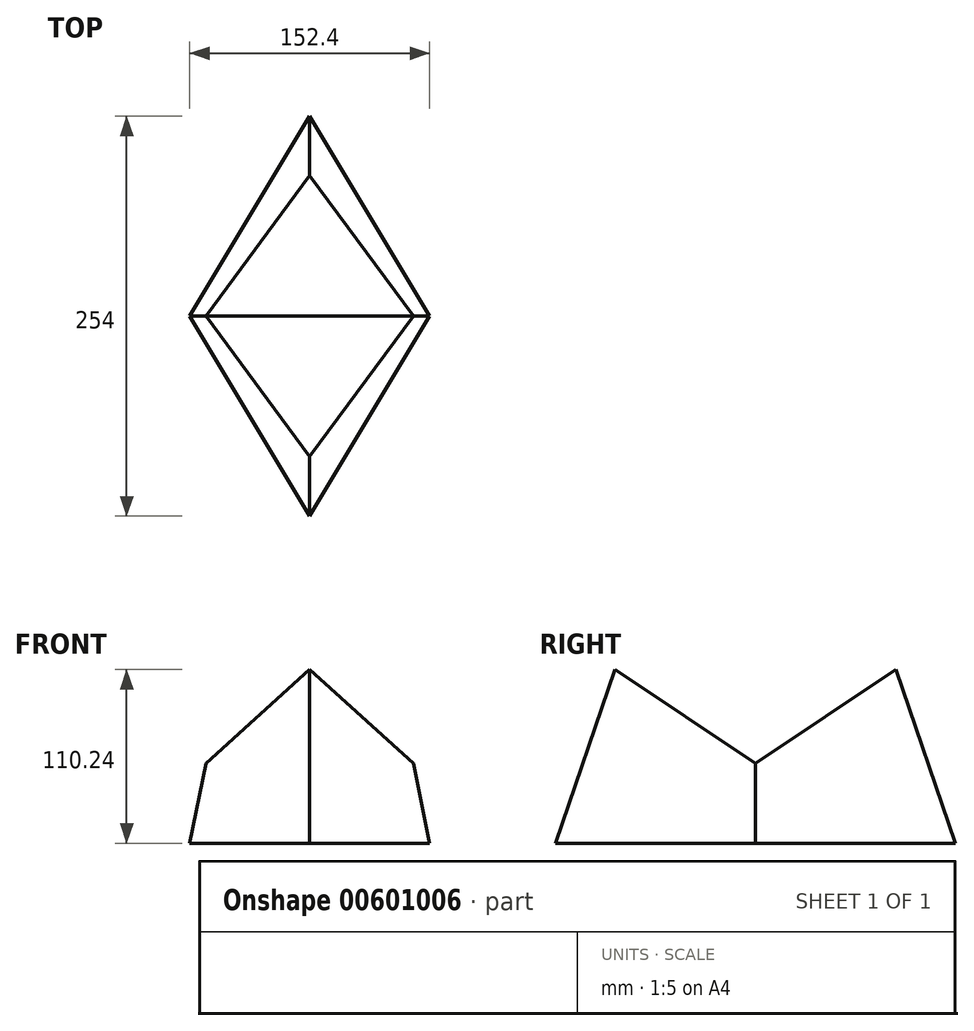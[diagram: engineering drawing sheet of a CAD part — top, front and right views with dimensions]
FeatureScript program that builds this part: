
annotation { "Feature Type Name" : "Feature", "Feature Type Description" : "" }
export const myFeature = defineFeature(function(context is Context, id is Id, definition is map)
    precondition{}
    {
        {
            var Q0;
            Q0=qCreatedBy(makeId("Top.planeOp"),FACE);
            var sketch = newSketch(context, id + "F0", { "sketchPlane" : qUnion([Q0])});
            skLineSegment(sketch, "E0", {"start": v(-76.2, 0) * mm, "end": v(0, 127) * mm});
            skLineSegment(sketch, "E1", {"start": v(0, 127) * mm, "end": v(76.2, 0) * mm});
            skLineSegment(sketch, "E2", {"start": v(76.2, 0) * mm, "end": v(0, -127) * mm});
            skLineSegment(sketch, "E3", {"start": v(-76.2, 0) * mm, "end": v(0, -127) * mm});
            skSolve(sketch);
        }
        {
            var Q0;
            Q0 = qSketchRegion(id + "F0", true);
            extrude(context, id + "F1", {"entities" : qUnion([Q0]), "depth" : 110.24 * mm, "offsetDistance" : 25.4 * mm, "hasDraft" : true, "draftAngle" : 10 * degree, "draftPullDirection" : true});
        }
        {
            var Q0;
            Q0=qCreatedBy(makeId("Right.planeOp"),FACE);
            var sketch = newSketch(context, id + "F2", { "sketchPlane" : qUnion([Q0])});
            skLineSegment(sketch, "E4", {"start": v(89.22, 110.24) * mm, "end": v(0, 50.8) * mm});
            skLineSegment(sketch, "E5", {"start": v(0, 50.8) * mm, "end": v(-89.22, 110.24) * mm});
            skLineSegment(sketch, "E6", {"start": v(-89.22, 110.24) * mm, "end": v(89.22, 110.24) * mm});
            skSolve(sketch);
        }
        {
            var Q0;
            Q0 = qSketchRegion(id + "F2", true);
            extrude(context, id + "F3", {"entities" : qUnion([Q0]), "operationType" : NewBodyOperationType.REMOVE, "oppositeDirection" : true, "depth" : 76.45 * mm, "offsetDistance" : 25.4 * mm, "hasSecondDirection" : true, "secondDirectionOppositeDirection" : false, "secondDirectionDepth" : 91.44 * mm});
        }
    });
